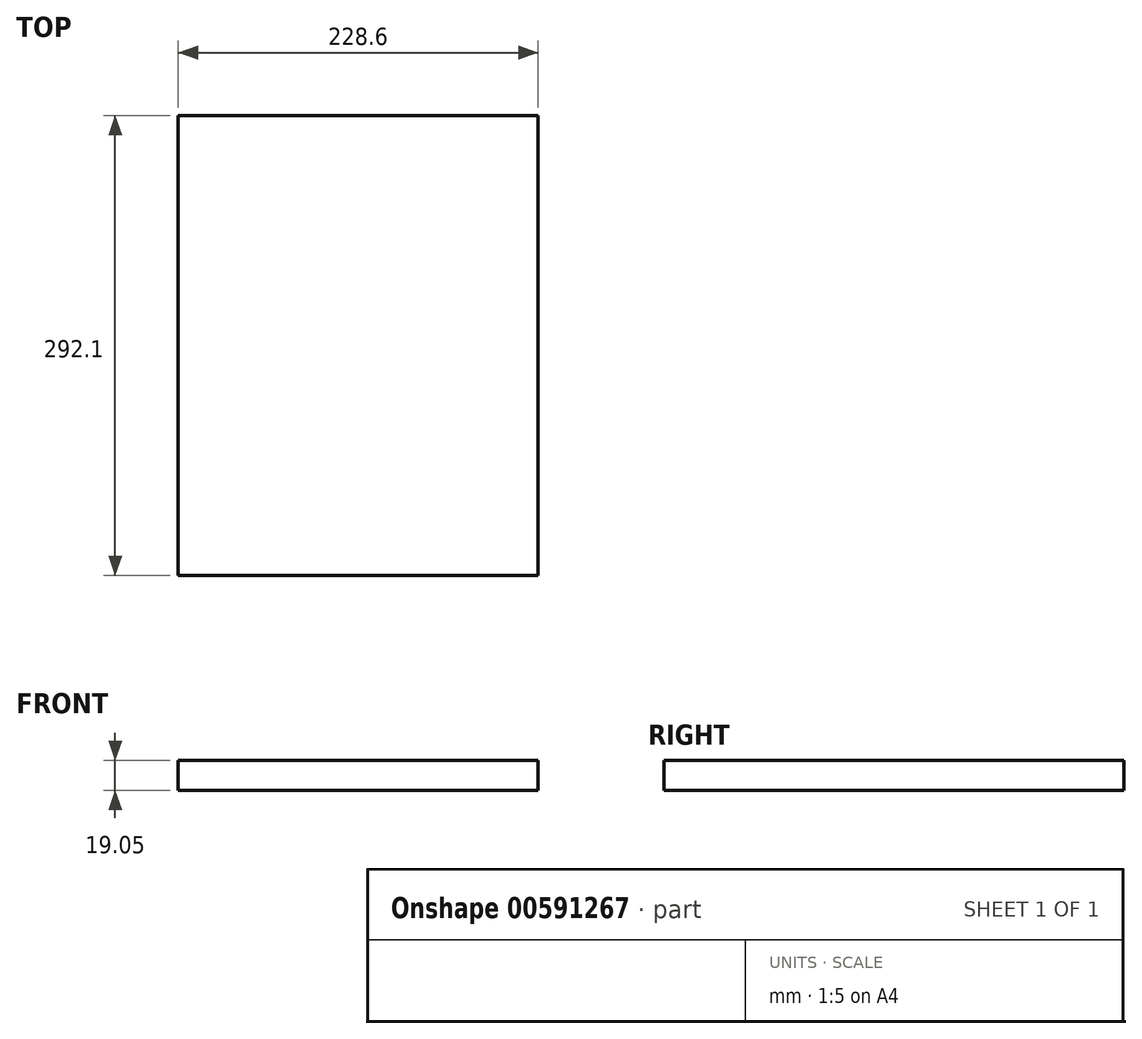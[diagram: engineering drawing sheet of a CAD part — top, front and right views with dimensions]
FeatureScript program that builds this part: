
annotation { "Feature Type Name" : "Feature", "Feature Type Description" : "" }
export const myFeature = defineFeature(function(context is Context, id is Id, definition is map)
    precondition{}
    {
        {
            var Q0;
            Q0=qCreatedBy(makeId("Top.planeOp"),FACE);
            var sketch = newSketch(context, id + "F0", { "sketchPlane" : qUnion([Q0])});
            skLineSegment(sketch, "E0.bottom", {"start": v(114.3, -146.05) * mm, "end": v(-114.3, -146.05) * mm});
            skLineSegment(sketch, "E0.top", {"start": v(114.3, 146.05) * mm, "end": v(-114.3, 146.05) * mm});
            skLineSegment(sketch, "E0.left", {"start": v(114.3, -146.05) * mm, "end": v(114.3, 146.05) * mm});
            skLineSegment(sketch, "E0.right", {"start": v(-114.3, -146.05) * mm, "end": v(-114.3, 146.05) * mm});
            skPoint(sketch, "E0.middle", {"position": v(0, 0) * mm});
            skSolve(sketch);
        }
        {
            var Q0;
            Q0 = qSketchRegion(id + "F0", true);
            extrude(context, id + "F1", {"entities" : qUnion([Q0]), "depth" : 19.05 * mm, "offsetDistance" : 25.4 * mm});
        }
    });
